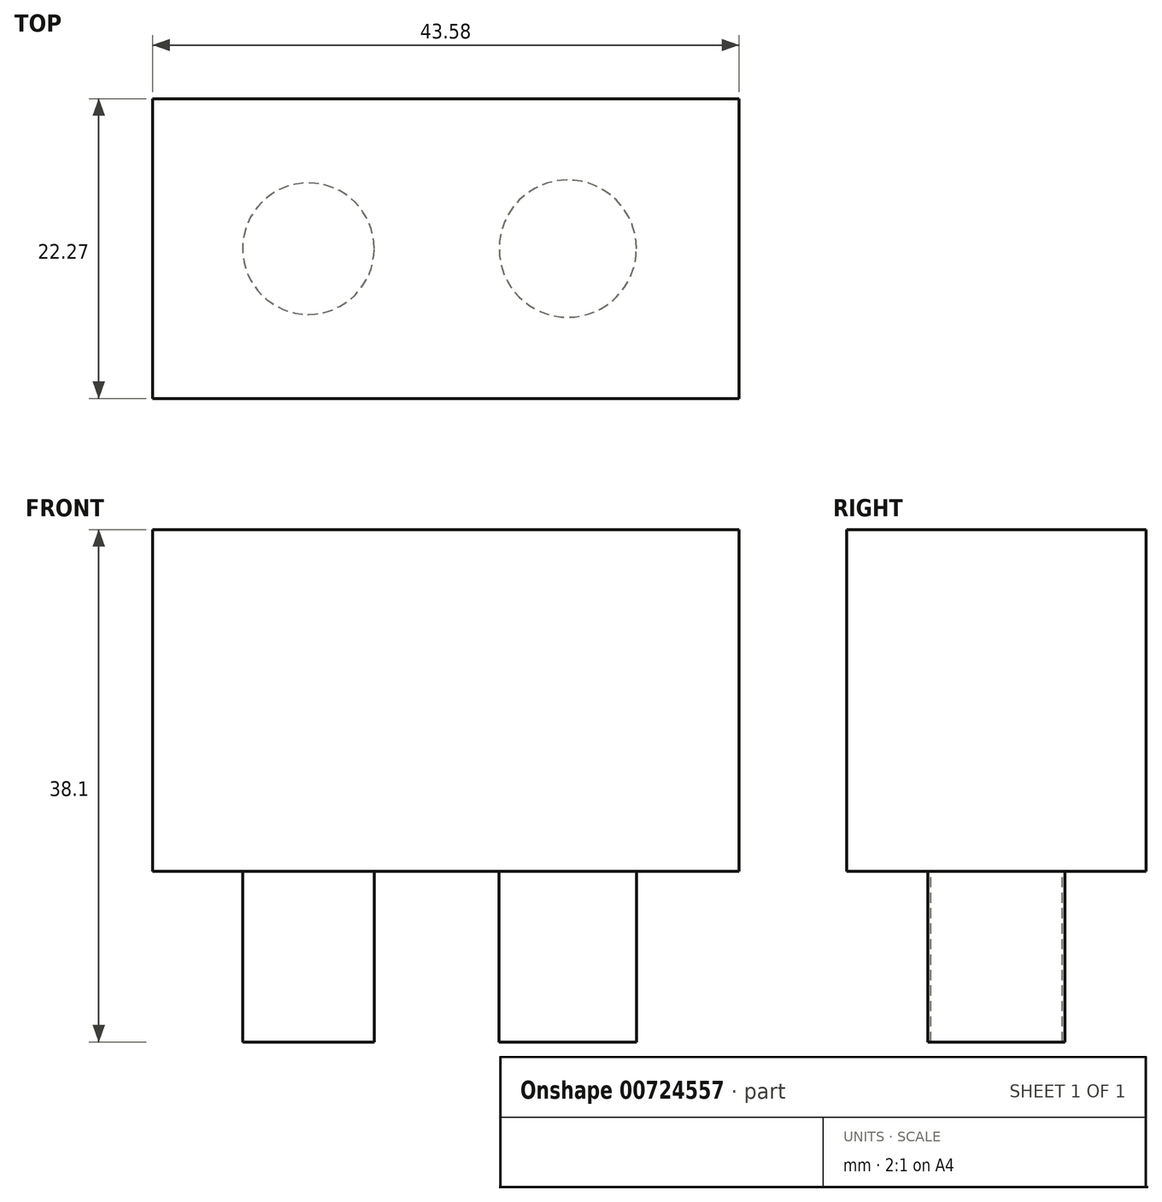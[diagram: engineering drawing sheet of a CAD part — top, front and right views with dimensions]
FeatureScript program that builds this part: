
annotation { "Feature Type Name" : "Feature", "Feature Type Description" : "" }
export const myFeature = defineFeature(function(context is Context, id is Id, definition is map)
    precondition{}
    {
        {
            var Q0;
            Q0=qCreatedBy(makeId("Top.planeOp"),FACE);
            var sketch = newSketch(context, id + "F0", { "sketchPlane" : qUnion([Q0])});
            skLineSegment(sketch, "E0.bottom", {"start": v(0, 0) * mm, "end": v(-43.58, 0) * mm});
            skLineSegment(sketch, "E0.top", {"start": v(0, 22.27) * mm, "end": v(-43.58, 22.27) * mm});
            skLineSegment(sketch, "E0.left", {"start": v(0, 0) * mm, "end": v(0, 22.27) * mm});
            skLineSegment(sketch, "E0.right", {"start": v(-43.58, 0) * mm, "end": v(-43.58, 22.27) * mm});
            skCircle(sketch, "E1", {"center": v(-32, 11.14) * mm, "radius": 4.9 * mm});
            skPoint(sketch, "E1.centerSnap0", {"position": v(-43.58, 11.14) * mm});
            skCircle(sketch, "E2", {"center": v(-12.72, 11.14) * mm, "radius": 5.1 * mm});
            skSolve(sketch);
        }
        {
            var Q0;
            Q0=makeQuery(id+"F0.imprint","IMPRINT",FACE,{"disambiguationData":[TD([[makeQuery(id+"F0.imprint","IMPRINT",EDGE,{"derivedFrom":sQuery(id+"F0.wireOp",EDGE,"E0.bottom")}),-1.0]])]});
            var Q1;
            Q1=makeQuery(id+"F0.imprint","IMPRINT",FACE,{"disambiguationData":[TD([[makeQuery(id+"F0.imprint","IMPRINT",EDGE,{"derivedFrom":sQuery(id+"F0.wireOp",EDGE,"E1")}),1.0]])]});
            var Q2;
            Q2=makeQuery(id+"F0.imprint","IMPRINT",FACE,{"disambiguationData":[TD([[makeQuery(id+"F0.imprint","IMPRINT",EDGE,{"derivedFrom":sQuery(id+"F0.wireOp",EDGE,"E2")}),1.0]])]});
            extrude(context, id + "F1", {"entities" : qUnion([Q0, Q1, Q2]), "depth" : 25.4 * mm, "offsetDistance" : 25.4 * mm});
        }
        {
            var Q0;
            Q0=makeQuery(id+"F0.imprint","IMPRINT",FACE,{"disambiguationData":[TD([[makeQuery(id+"F0.imprint","IMPRINT",EDGE,{"derivedFrom":sQuery(id+"F0.wireOp",EDGE,"E1")}),1.0]])]});
            var Q1;
            Q1=makeQuery(id+"F0.imprint","IMPRINT",FACE,{"disambiguationData":[TD([[makeQuery(id+"F0.imprint","IMPRINT",EDGE,{"derivedFrom":sQuery(id+"F0.wireOp",EDGE,"E2")}),1.0]])]});
            extrude(context, id + "F2", {"entities" : qUnion([Q0, Q1]), "operationType" : NewBodyOperationType.ADD, "oppositeDirection" : true, "depth" : 12.7 * mm, "offsetDistance" : 25.4 * mm});
        }
    });
